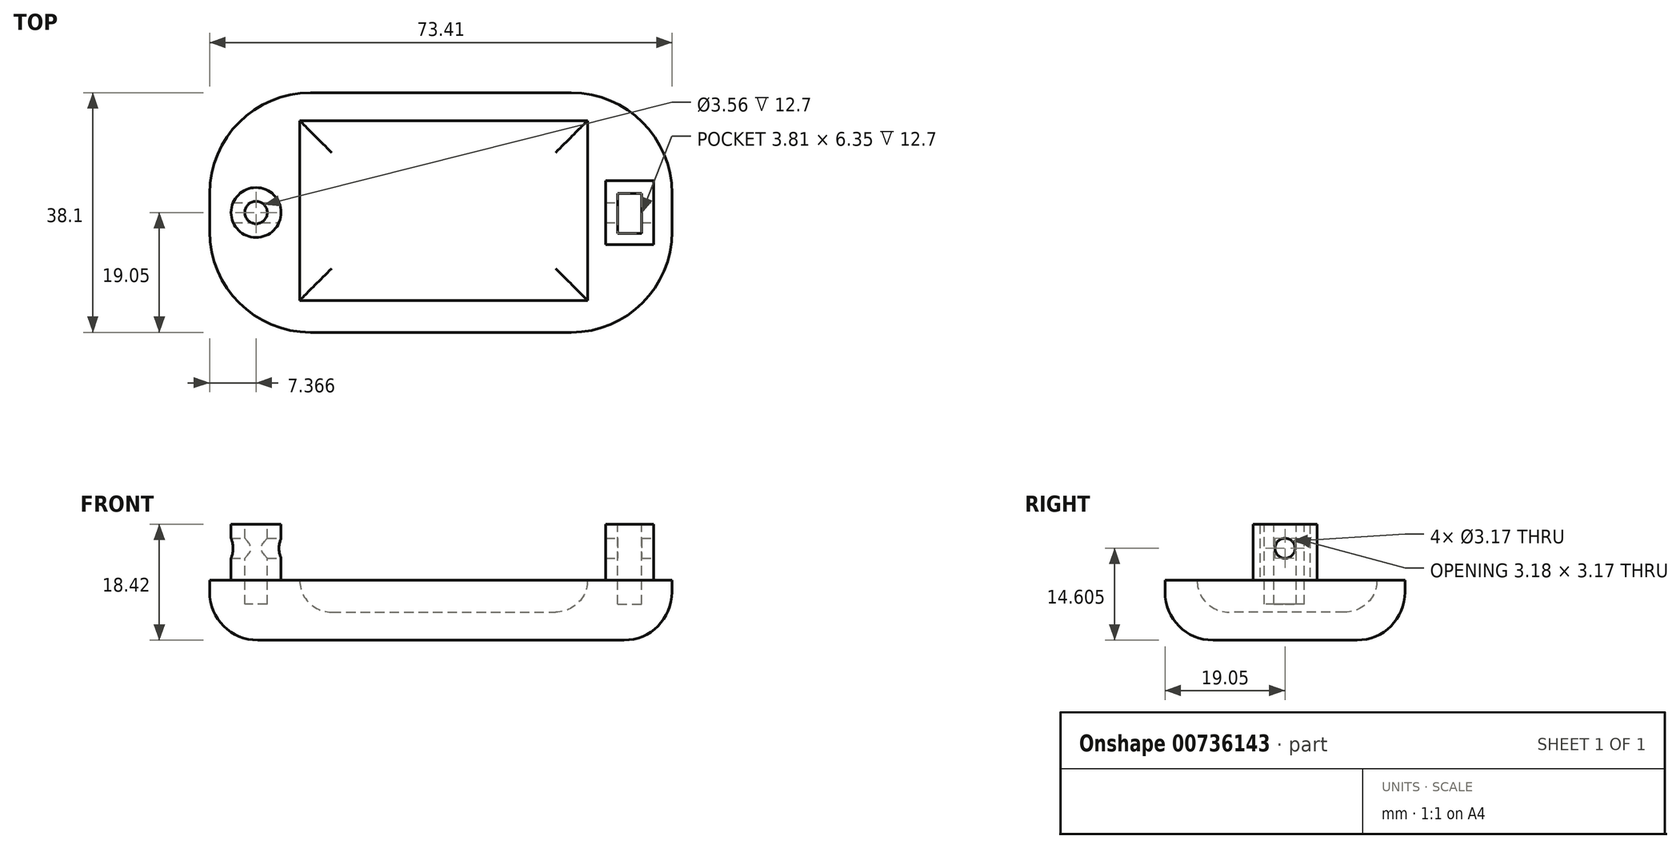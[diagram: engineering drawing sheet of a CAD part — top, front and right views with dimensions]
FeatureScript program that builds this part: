
annotation { "Feature Type Name" : "Feature", "Feature Type Description" : "" }
export const myFeature = defineFeature(function(context is Context, id is Id, definition is map)
    precondition{}
    {
        {
            var Q0;
            Q0=qCreatedBy(makeId("Top.planeOp"),FACE);
            var sketch = newSketch(context, id + "F0", { "sketchPlane" : qUnion([Q0])});
            skLineSegment(sketch, "E0.bottom", {"start": v(0, 0) * mm, "end": v(73.4, 0) * mm});
            skLineSegment(sketch, "E0.top", {"start": v(0, 38.1) * mm, "end": v(73.4, 38.1) * mm});
            skLineSegment(sketch, "E0.left", {"start": v(0, 0) * mm, "end": v(0, 38.1) * mm});
            skLineSegment(sketch, "E0.right", {"start": v(73.4, 0) * mm, "end": v(73.4, 38.1) * mm});
            skSolve(sketch);
        }
        {
            var Q0;
            Q0 = qSketchRegion(id + "F0", true);
            extrude(context, id + "F1", {"entities" : qUnion([Q0]), "depth" : 9.52 * mm, "offsetDistance" : 25.4 * mm});
        }
        {
            var Q0;
            Q0=makeQuery(id+"F1.opExtrude","SWEPT_EDGE",EDGE,{"disambiguationData":[OSD([sQuery(id+"F0.wireOp",EDGE,"E0.top"),sQuery(id+"F0.wireOp",EDGE,"E0.left")])]});
            var Q1;
            Q1=makeQuery(id+"F1.opExtrude","SWEPT_EDGE",EDGE,{"disambiguationData":[OSD([sQuery(id+"F0.wireOp",EDGE,"E0.bottom"),sQuery(id+"F0.wireOp",EDGE,"E0.left")])]});
            var Q2;
            Q2=makeQuery(id+"F1.opExtrude","SWEPT_EDGE",EDGE,{"disambiguationData":[OSD([sQuery(id+"F0.wireOp",EDGE,"E0.top"),sQuery(id+"F0.wireOp",EDGE,"E0.right")])]});
            var Q3;
            Q3=makeQuery(id+"F1.opExtrude","SWEPT_EDGE",EDGE,{"disambiguationData":[OSD([sQuery(id+"F0.wireOp",EDGE,"E0.bottom"),sQuery(id+"F0.wireOp",EDGE,"E0.right")])]});
            fillet(context, id + "F2", {"entities" : qUnion([Q0, Q1, Q2, Q3]), "radius" : 16 * mm, "tangentPropagation" : true, "allowEdgeOverflow" : false});
        }
        {
            var Q0;
            Q0=makeQuery(id+"F1.opExtrude","CAP_FACE",FACE,{"disambiguationData":[OSD([sQuery(id+"F0.wireOp",EDGE,"E0.bottom"),sQuery(id+"F0.wireOp",EDGE,"E0.top"),sQuery(id+"F0.wireOp",EDGE,"E0.left"),sQuery(id+"F0.wireOp",EDGE,"E0.right")])],"isStart":false});
            var sketch = newSketch(context, id + "F3", { "sketchPlane" : qUnion([Q0])});
            skCircle(sketch, "E1", {"center": v(7.37, 19.05) * mm, "radius": 3.97 * mm});
            skLineSegment(sketch, "E2.bottom", {"start": v(62.87, 24.13) * mm, "end": v(70.48, 24.13) * mm});
            skLineSegment(sketch, "E2.top", {"start": v(62.87, 13.97) * mm, "end": v(70.48, 13.97) * mm});
            skLineSegment(sketch, "E2.left", {"start": v(62.87, 24.13) * mm, "end": v(62.87, 13.97) * mm});
            skLineSegment(sketch, "E2.right", {"start": v(70.48, 24.13) * mm, "end": v(70.48, 13.97) * mm});
            skSolve(sketch);
        }
        {
            var Q0;
            Q0 = qSketchRegion(id + "F3", true);
            extrude(context, id + "F4", {"entities" : qUnion([Q0]), "operationType" : NewBodyOperationType.ADD, "depth" : 8.9 * mm, "offsetDistance" : 25.4 * mm});
        }
        {
            var Q0;
            Q0=makeQuery(id+"F4.opExtrude","SWEPT_FACE",FACE,{"disambiguationData":[OSD([sQuery(id+"F3.wireOp",EDGE,"E2.right")])]});
            var sketch = newSketch(context, id + "F5", { "sketchPlane" : qUnion([Q0])});
            skCircle(sketch, "E3", {"center": v(19.05, 14.6) * mm, "radius": 1.59 * mm});
            skPoint(sketch, "E3.centerSnap0", {"position": v(19.05, 9.53) * mm});
            skSolve(sketch);
        }
        {
            var Q0;
            Q0 = qSketchRegion(id + "F5", true);
            extrude(context, id + "F6", {"entities" : qUnion([Q0]), "operationType" : NewBodyOperationType.REMOVE, "oppositeDirection" : true, "depth" : 68.58 * mm, "offsetDistance" : 25.4 * mm});
        }
        {
            var Q0;
            Q0=makeQuery(id+"F4.opExtrude","CAP_FACE",FACE,{"disambiguationData":[OSD([sQuery(id+"F3.wireOp",EDGE,"E2.bottom"),sQuery(id+"F3.wireOp",EDGE,"E2.top"),sQuery(id+"F3.wireOp",EDGE,"E2.left"),sQuery(id+"F3.wireOp",EDGE,"E2.right")])],"isStart":false});
            var sketch = newSketch(context, id + "F7", { "sketchPlane" : qUnion([Q0])});
            skCircle(sketch, "E4", {"center": v(7.37, 19.05) * mm, "radius": 1.78 * mm});
            skLineSegment(sketch, "E5.bottom", {"start": v(64.77, 22.1) * mm, "end": v(68.58, 22.1) * mm});
            skLineSegment(sketch, "E5.top", {"start": v(64.77, 15.75) * mm, "end": v(68.58, 15.75) * mm});
            skLineSegment(sketch, "E5.left", {"start": v(64.77, 22.1) * mm, "end": v(64.77, 15.75) * mm});
            skLineSegment(sketch, "E5.right", {"start": v(68.58, 22.1) * mm, "end": v(68.58, 15.75) * mm});
            skSolve(sketch);
        }
        {
            var Q0;
            Q0 = qSketchRegion(id + "F7", true);
            extrude(context, id + "F8", {"entities" : qUnion([Q0]), "operationType" : NewBodyOperationType.REMOVE, "oppositeDirection" : true, "depth" : 12.7 * mm, "offsetDistance" : 25.4 * mm});
        }
        {
            var Q0;
            Q0=makeQuery(id+"F1.opExtrude","CAP_EDGE",EDGE,{"disambiguationData":[OSD([sQuery(id+"F0.wireOp",EDGE,"E0.bottom")])],"isStart":true});
            fillet(context, id + "F9", {"entities" : qUnion([Q0]), "radius" : 7.62 * mm, "tangentPropagation" : true, "allowEdgeOverflow" : false});
        }
        {
            var Q0;
            Q0=makeQuery(id+"F1.opExtrude","CAP_FACE",FACE,{"disambiguationData":[OSD([sQuery(id+"F0.wireOp",EDGE,"E0.bottom"),sQuery(id+"F0.wireOp",EDGE,"E0.top"),sQuery(id+"F0.wireOp",EDGE,"E0.left"),sQuery(id+"F0.wireOp",EDGE,"E0.right")])],"isStart":false});
            var sketch = newSketch(context, id + "F10", { "sketchPlane" : qUnion([Q0])});
            skLineSegment(sketch, "E6.bottom", {"start": v(14.28, 33.66) * mm, "end": v(60, 33.66) * mm});
            skLineSegment(sketch, "E6.top", {"start": v(14.28, 5.08) * mm, "end": v(60, 5.08) * mm});
            skLineSegment(sketch, "E6.left", {"start": v(14.28, 33.66) * mm, "end": v(14.28, 5.08) * mm});
            skLineSegment(sketch, "E6.right", {"start": v(60, 33.66) * mm, "end": v(60, 5.08) * mm});
            skSolve(sketch);
        }
        {
            var Q0;
            Q0 = qSketchRegion(id + "F10", true);
            extrude(context, id + "F11", {"entities" : qUnion([Q0]), "operationType" : NewBodyOperationType.REMOVE, "oppositeDirection" : true, "depth" : 5.08 * mm, "offsetDistance" : 25.4 * mm});
        }
        {
            var Q0;
            Q0=makeQuery(id+"F11.boolean.opBoolean","COPY",FACE,{"derivedFrom":makeQuery(id+"F11.opExtrude","CAP_FACE",FACE,{"disambiguationData":[OSD([sQuery(id+"F10.wireOp",EDGE,"E6.bottom"),sQuery(id+"F10.wireOp",EDGE,"E6.top"),sQuery(id+"F10.wireOp",EDGE,"E6.left"),sQuery(id+"F10.wireOp",EDGE,"E6.right")])],"isStart":false})});
            fillet(context, id + "F12", {"entities" : qUnion([Q0]), "radius" : 5.08 * mm, "tangentPropagation" : true, "allowEdgeOverflow" : false});
        }
    });
